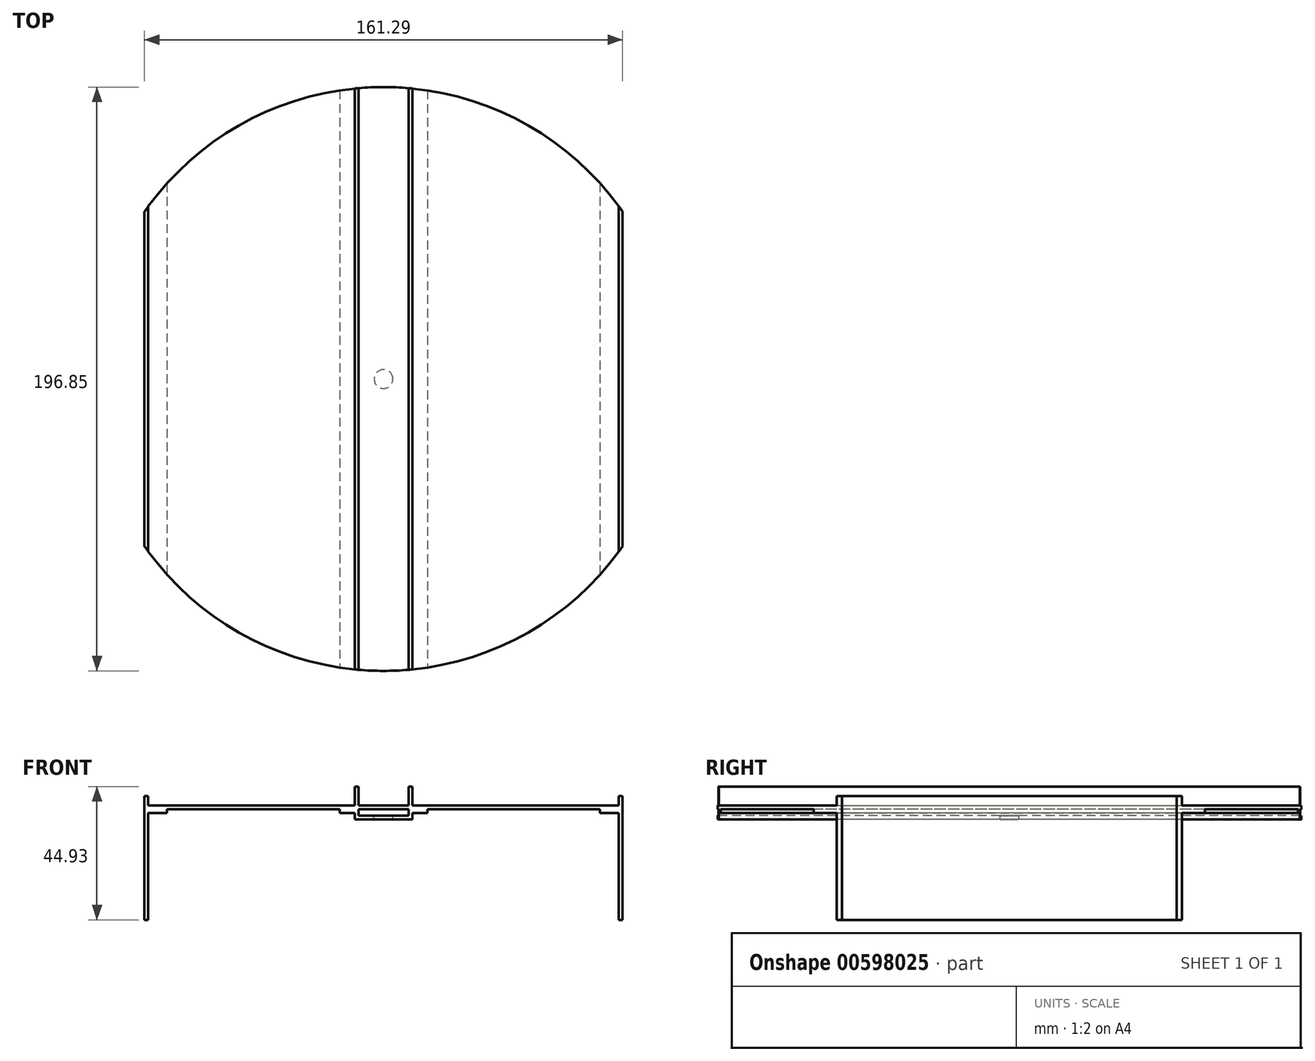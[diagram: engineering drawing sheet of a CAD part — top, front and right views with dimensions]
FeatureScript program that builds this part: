
annotation { "Feature Type Name" : "Feature", "Feature Type Description" : "" }
export const myFeature = defineFeature(function(context is Context, id is Id, definition is map)
    precondition{}
    {
        {
            var Q0;
            Q0=qCreatedBy(makeId("Top.planeOp"),FACE);
            var sketch = newSketch(context, id + "F0", { "sketchPlane" : qUnion([Q0])});
            skCircle(sketch, "E0", {"center": v(0, 0) * mm, "radius": 98.43 * mm, "construction": true});
            skArc(sketch, "E1", {"start": v(-79.38, 58.2) * mm, "mid": v(0, 98.43) * mm, "end": v(79.38, 58.2) * mm});
            skArc(sketch, "E2", {"start": v(79.38, -58.2) * mm, "mid": v(0, -98.43) * mm, "end": v(-79.38, -58.2) * mm});
            skLineSegment(sketch, "E3", {"start": v(-79.38, 58.2) * mm, "end": v(-79.38, -58.2) * mm});
            skLineSegment(sketch, "E4", {"start": v(79.38, 58.2) * mm, "end": v(79.38, -58.2) * mm});
            skLineSegment(sketch, "E5", {"start": v(0, 98.43) * mm, "end": v(0, -98.43) * mm, "construction": true});
            skLineSegment(sketch, "E6", {"start": v(-8.47, 98.06) * mm, "end": v(-8.47, -98.06) * mm});
            skLineSegment(sketch, "E7", {"start": v(-9.74, 97.94) * mm, "end": v(-9.74, -97.94) * mm});
            skLineSegment(sketch, "E8", {"start": v(8.47, 98.06) * mm, "end": v(8.47, -98.06) * mm});
            skLineSegment(sketch, "E9", {"start": v(9.74, 97.94) * mm, "end": v(9.74, -97.94) * mm});
            skArc(sketch, "E10", {"start": v(-73.14, 65.86) * mm, "mid": v(-69.6, 69.6) * mm, "end": v(-65.86, 73.14) * mm});
            skArc(sketch, "E11", {"start": v(66.5, 72.57) * mm, "mid": v(69.6, 69.6) * mm, "end": v(72.57, 66.5) * mm});
            skArc(sketch, "E12", {"start": v(18.66, -96.64) * mm, "mid": v(-25.47, 95.07) * mm, "end": v(32.16, -93.02) * mm});
            skArc(sketch, "E13", {"start": v(-18.63, -96.65) * mm, "mid": v(-25.47, -95.07) * mm, "end": v(-32.2, -93.01) * mm});
            skArc(sketch, "E14", {"start": v(-30.41, 93.6) * mm, "mid": v(-25.47, 95.07) * mm, "end": v(-20.46, 96.27) * mm});
            skArc(sketch, "E15", {"start": v(20.46, 96.27) * mm, "mid": v(25.47, 95.07) * mm, "end": v(30.41, 93.6) * mm});
            skArc(sketch, "E16", {"start": v(64.56, -74.3) * mm, "mid": v(-69.6, 69.6) * mm, "end": v(74.3, -64.56) * mm});
            skArc(sketch, "E17", {"start": v(-72.22, -66.87) * mm, "mid": v(-69.6, -69.6) * mm, "end": v(-66.87, -72.22) * mm});
            skLineSegment(sketch, "E18", {"start": v(-69.6, 69.6) * mm, "end": v(-69.6, -69.6) * mm, "construction": true});
            skLineSegment(sketch, "E19", {"start": v(-69.6, -69.6) * mm, "end": v(69.6, -69.6) * mm, "construction": true});
            skLineSegment(sketch, "E20", {"start": v(69.6, -69.6) * mm, "end": v(69.6, 69.6) * mm, "construction": true});
            skLineSegment(sketch, "E21", {"start": v(69.6, 69.6) * mm, "end": v(-69.6, 69.6) * mm, "construction": true});
            skLineSegment(sketch, "E22", {"start": v(-25.47, 95.07) * mm, "end": v(-25.47, -95.07) * mm, "construction": true});
            skLineSegment(sketch, "E23", {"start": v(-25.47, -95.07) * mm, "end": v(25.47, -95.07) * mm, "construction": true});
            skLineSegment(sketch, "E24", {"start": v(25.47, -95.07) * mm, "end": v(25.47, 95.07) * mm, "construction": true});
            skLineSegment(sketch, "E25", {"start": v(25.47, 95.07) * mm, "end": v(-25.47, 95.07) * mm, "construction": true});
            skLineSegment(sketch, "E26", {"start": v(0, 0) * mm, "end": v(-69.6, 69.6) * mm, "construction": true});
            skLineSegment(sketch, "E27", {"start": v(0, 0) * mm, "end": v(-25.47, 95.07) * mm, "construction": true});
            skLineSegment(sketch, "E28", {"start": v(-69.6, 69.6) * mm, "end": v(-52.3, 86.89) * mm, "construction": true});
            skLineSegment(sketch, "E29", {"start": v(-25.47, 95.07) * mm, "end": v(-17.64, 97.17) * mm, "construction": true});
            skLineSegment(sketch, "E30", {"start": v(25.47, 95.07) * mm, "end": v(35.03, 92.51) * mm, "construction": true});
            skLineSegment(sketch, "E31", {"start": v(69.6, 69.6) * mm, "end": v(84.24, 54.95) * mm, "construction": true});
            skLineSegment(sketch, "E32", {"start": v(69.6, -69.6) * mm, "end": v(50.03, -89.17) * mm, "construction": true});
            skLineSegment(sketch, "E33", {"start": v(25.47, -95.07) * mm, "end": v(7.54, -99.88) * mm, "construction": true});
            skLineSegment(sketch, "E34", {"start": v(-25.47, -95.07) * mm, "end": v(-73.92, -82.09) * mm, "construction": true});
            skLineSegment(sketch, "E35", {"start": v(-69.6, -69.6) * mm, "end": v(-126.46, -12.73) * mm, "construction": true});
            skLineSegment(sketch, "E36", {"start": v(0, 0) * mm, "end": v(-73.14, 65.86) * mm, "construction": true});
            skLineSegment(sketch, "E37", {"start": v(0, 0) * mm, "end": v(-30.41, 93.6) * mm, "construction": true});
            skLineSegment(sketch, "E38", {"start": v(0, 0) * mm, "end": v(30.41, 93.6) * mm, "construction": true});
            skLineSegment(sketch, "E39", {"start": v(0, 0) * mm, "end": v(72.57, 66.5) * mm, "construction": true});
            skLineSegment(sketch, "E40", {"start": v(0, 0) * mm, "end": v(74.3, -64.56) * mm, "construction": true});
            skLineSegment(sketch, "E41", {"start": v(0, 0) * mm, "end": v(32.16, -93.02) * mm, "construction": true});
            skLineSegment(sketch, "E42", {"start": v(0, 0) * mm, "end": v(-32.2, -93.01) * mm, "construction": true});
            skLineSegment(sketch, "E43", {"start": v(0, 0) * mm, "end": v(-72.22, -66.87) * mm, "construction": true});
            skLineSegment(sketch, "E44", {"start": v(0, 0) * mm, "end": v(25.47, 95.07) * mm, "construction": true});
            skLineSegment(sketch, "E45", {"start": v(0, 0) * mm, "end": v(69.6, 69.6) * mm, "construction": true});
            skLineSegment(sketch, "E46", {"start": v(0, 0) * mm, "end": v(69.6, -69.6) * mm, "construction": true});
            skLineSegment(sketch, "E47", {"start": v(0, 0) * mm, "end": v(25.47, -95.07) * mm, "construction": true});
            skLineSegment(sketch, "E48", {"start": v(0, 0) * mm, "end": v(-25.47, -95.07) * mm, "construction": true});
            skLineSegment(sketch, "E49", {"start": v(0, 0) * mm, "end": v(-69.6, -69.6) * mm, "construction": true});
            skLineSegment(sketch, "E50", {"start": v(-73.14, 65.86) * mm, "end": v(-69.82, 62.54) * mm});
            skLineSegment(sketch, "E51", {"start": v(-69.82, 62.54) * mm, "end": v(-62.54, 69.82) * mm});
            skLineSegment(sketch, "E52", {"start": v(-62.54, 69.82) * mm, "end": v(-65.86, 73.14) * mm});
            skLineSegment(sketch, "E53", {"start": v(-69.6, 69.6) * mm, "end": v(-67.89, 67.89) * mm, "construction": true});
            skLineSegment(sketch, "E54", {"start": v(-67.89, 67.89) * mm, "end": v(-66.18, 66.18) * mm, "construction": true});
            skLineSegment(sketch, "E55", {"start": v(-67.13, 71.98) * mm, "end": v(-64.97, 69.82) * mm});
            skLineSegment(sketch, "E56", {"start": v(-64.97, 69.82) * mm, "end": v(-69.82, 64.97) * mm});
            skLineSegment(sketch, "E57", {"start": v(-69.82, 64.97) * mm, "end": v(-71.98, 67.13) * mm});
            skLineSegment(sketch, "E58", {"start": v(-69.82, 64.97) * mm, "end": v(-71.04, 63.76) * mm, "construction": true});
            skLineSegment(sketch, "E59", {"start": v(-64.97, 69.82) * mm, "end": v(-63.76, 71.04) * mm, "construction": true});
            skLineSegment(sketch, "E60", {"start": v(-69.82, 64.97) * mm, "end": v(-68.6, 63.76) * mm, "construction": true});
            skLineSegment(sketch, "E61", {"start": v(-30.41, 93.6) * mm, "end": v(-29.2, 89.07) * mm});
            skLineSegment(sketch, "E62", {"start": v(-29.2, 89.07) * mm, "end": v(-19.25, 91.74) * mm});
            skLineSegment(sketch, "E63", {"start": v(-19.25, 91.74) * mm, "end": v(-20.46, 96.27) * mm});
            skLineSegment(sketch, "E64", {"start": v(-28.77, 94.13) * mm, "end": v(-27.98, 91.18) * mm});
            skLineSegment(sketch, "E65", {"start": v(-27.98, 91.18) * mm, "end": v(-21.36, 92.96) * mm});
            skLineSegment(sketch, "E66", {"start": v(-21.36, 92.96) * mm, "end": v(-22.15, 95.9) * mm});
            skLineSegment(sketch, "E67", {"start": v(-27.98, 91.18) * mm, "end": v(-29.65, 90.74) * mm, "construction": true});
            skLineSegment(sketch, "E68", {"start": v(-27.98, 91.18) * mm, "end": v(-27.54, 89.52) * mm, "construction": true});
            skLineSegment(sketch, "E69", {"start": v(-21.36, 92.96) * mm, "end": v(-19.7, 93.4) * mm, "construction": true});
            skLineSegment(sketch, "E70", {"start": v(20.46, 96.27) * mm, "end": v(19.25, 91.74) * mm});
            skLineSegment(sketch, "E71", {"start": v(19.25, 91.74) * mm, "end": v(29.2, 89.07) * mm});
            skLineSegment(sketch, "E72", {"start": v(29.2, 89.07) * mm, "end": v(30.41, 93.6) * mm});
            skLineSegment(sketch, "E73", {"start": v(22.15, 95.9) * mm, "end": v(21.36, 92.96) * mm});
            skLineSegment(sketch, "E74", {"start": v(21.36, 92.96) * mm, "end": v(27.98, 91.18) * mm});
            skLineSegment(sketch, "E75", {"start": v(27.98, 91.18) * mm, "end": v(28.77, 94.13) * mm});
            skLineSegment(sketch, "E76", {"start": v(21.36, 92.96) * mm, "end": v(19.7, 93.4) * mm, "construction": true});
            skLineSegment(sketch, "E77", {"start": v(27.98, 91.18) * mm, "end": v(29.65, 90.74) * mm, "construction": true});
            skLineSegment(sketch, "E78", {"start": v(21.36, 92.96) * mm, "end": v(20.91, 91.3) * mm, "construction": true});
            skSolve(sketch);
        }
        {
            var Q0;
            {var subQ0=sQuery(id+"F0.wireOp",EDGE,"E3");Q0=makeQuery(id+"F0.imprint","IMPRINT",FACE,{"disambiguationData":[TD([[makeQuery(id+"F0.imprint","IMPRINT",EDGE,{"derivedFrom":subQ0}),1.0]])]});}
            var Q1;
            {var subQ0=sQuery(id+"F0.wireOp",EDGE,"E4");Q1=makeQuery(id+"F0.imprint","IMPRINT",FACE,{"disambiguationData":[TD([[makeQuery(id+"F0.imprint","IMPRINT",EDGE,{"derivedFrom":subQ0}),-1.0]])]});}
            var Q2;
            {var subQ0=sQuery(id+"F0.wireOp",EDGE,"E6");Q2=makeQuery(id+"F0.imprint","IMPRINT",FACE,{"disambiguationData":[TD([[makeQuery(id+"F0.imprint","IMPRINT",EDGE,{"derivedFrom":subQ0}),1.0]])]});}
            var Q3;
            {var subQ0=sQuery(id+"F0.wireOp",EDGE,"E6");Q3=makeQuery(id+"F0.imprint","IMPRINT",FACE,{"disambiguationData":[TD([[makeQuery(id+"F0.imprint","IMPRINT",EDGE,{"derivedFrom":subQ0}),-1.0]])]});}
            var Q4;
            {var subQ0=sQuery(id+"F0.wireOp",EDGE,"E8");Q4=makeQuery(id+"F0.imprint","IMPRINT",FACE,{"disambiguationData":[TD([[makeQuery(id+"F0.imprint","IMPRINT",EDGE,{"derivedFrom":subQ0}),1.0]])]});}
            var Q5;
            {var subQ0=sQuery(id+"F0.wireOp",EDGE,"E55");Q5=makeQuery(id+"F0.imprint","IMPRINT",FACE,{"disambiguationData":[TD([[makeQuery(id+"F0.imprint","IMPRINT",EDGE,{"derivedFrom":subQ0}),-1.0]])]});}
            var Q6;
            {var subQ0=sQuery(id+"F0.wireOp",EDGE,"E50");Q6=makeQuery(id+"F0.imprint","IMPRINT",FACE,{"disambiguationData":[TD([[makeQuery(id+"F0.imprint","IMPRINT",EDGE,{"derivedFrom":subQ0}),1.0]])]});}
            var Q7;
            {var subQ0=sQuery(id+"F0.wireOp",EDGE,"E61");Q7=makeQuery(id+"F0.imprint","IMPRINT",FACE,{"disambiguationData":[TD([[makeQuery(id+"F0.imprint","IMPRINT",EDGE,{"derivedFrom":subQ0}),1.0]])]});}
            var Q8;
            {var subQ0=sQuery(id+"F0.wireOp",EDGE,"E64");Q8=makeQuery(id+"F0.imprint","IMPRINT",FACE,{"disambiguationData":[TD([[makeQuery(id+"F0.imprint","IMPRINT",EDGE,{"derivedFrom":subQ0}),1.0]])]});}
            var Q9;
            {var subQ0=sQuery(id+"F0.wireOp",EDGE,"E70");Q9=makeQuery(id+"F0.imprint","IMPRINT",FACE,{"disambiguationData":[TD([[makeQuery(id+"F0.imprint","IMPRINT",EDGE,{"derivedFrom":subQ0}),1.0]])]});}
            var Q10;
            {var subQ0=sQuery(id+"F0.wireOp",EDGE,"E73");Q10=makeQuery(id+"F0.imprint","IMPRINT",FACE,{"disambiguationData":[TD([[makeQuery(id+"F0.imprint","IMPRINT",EDGE,{"derivedFrom":subQ0}),1.0]])]});}
            extrude(context, id + "F1", {"entities" : qUnion([Q0, Q1, Q2, Q3, Q4, Q5, Q6, Q7, Q8, Q9, Q10]), "depth" : 1.27 * mm, "offsetDistance" : 25.4 * mm});
        }
        {
            var Q0;
            {var subQ0=sQuery(id+"F0.wireOp",EDGE,"E6");Q0=makeQuery(id+"F0.imprint","IMPRINT",FACE,{"disambiguationData":[TD([[makeQuery(id+"F0.imprint","IMPRINT",EDGE,{"derivedFrom":subQ0}),-1.0]])]});}
            var Q1;
            {var subQ0=sQuery(id+"F0.wireOp",EDGE,"E8");Q1=makeQuery(id+"F0.imprint","IMPRINT",FACE,{"disambiguationData":[TD([[makeQuery(id+"F0.imprint","IMPRINT",EDGE,{"derivedFrom":subQ0}),1.0]])]});}
            extrude(context, id + "F2", {"entities" : qUnion([Q0, Q1]), "operationType" : NewBodyOperationType.ADD, "depth" : 7.7 * mm, "offsetDistance" : 25.4 * mm});
        }
        {
            var Q0;
            Q0=qCreatedBy(makeId("Front.planeOp"),FACE);
            var sketch = newSketch(context, id + "F3", { "sketchPlane" : qUnion([Q0])});
            skLineSegment(sketch, "E79", {"start": v(0, 37.45) * mm, "end": v(0, -50.2) * mm, "construction": true});
            skSolve(sketch);
        }
        {
            var Q0;
            Q0=qCreatedBy(makeId("Top.planeOp"),FACE);
            var sketch = newSketch(context, id + "F4", { "sketchPlane" : qUnion([Q0])});
            skCircle(sketch, "E80", {"center": v(0, 0) * mm, "radius": 98.43 * mm, "construction": true});
            skLineSegment(sketch, "E81", {"start": v(0, 0) * mm, "end": v(-79.38, 0) * mm, "construction": true});
            skLineSegment(sketch, "E82", {"start": v(0, 0) * mm, "end": v(79.38, 0) * mm, "construction": true});
            skLineSegment(sketch, "E83", {"start": v(-79.38, 0) * mm, "end": v(-98.43, 0) * mm, "construction": true});
            skLineSegment(sketch, "E84", {"start": v(79.38, 0) * mm, "end": v(98.43, 0) * mm, "construction": true});
            skLineSegment(sketch, "E85", {"start": v(-79.38, 0) * mm, "end": v(-73.28, 0) * mm, "construction": true});
            skLineSegment(sketch, "E86", {"start": v(79.38, 0) * mm, "end": v(73.28, 0) * mm, "construction": true});
            skLineSegment(sketch, "E87", {"start": v(-79.38, 0) * mm, "end": v(-79.38, 58.2) * mm});
            skLineSegment(sketch, "E88", {"start": v(-79.38, 0) * mm, "end": v(-79.38, -58.2) * mm});
            skLineSegment(sketch, "E89", {"start": v(-73.28, 0) * mm, "end": v(-73.28, -65.7) * mm});
            skLineSegment(sketch, "E90", {"start": v(-73.28, 0) * mm, "end": v(-73.28, 65.7) * mm});
            skLineSegment(sketch, "E91", {"start": v(73.28, 0) * mm, "end": v(73.28, 65.7) * mm});
            skLineSegment(sketch, "E92", {"start": v(79.38, 0) * mm, "end": v(79.38, 58.2) * mm});
            skLineSegment(sketch, "E93", {"start": v(79.38, 0) * mm, "end": v(79.38, -58.2) * mm});
            skLineSegment(sketch, "E94", {"start": v(73.28, 0) * mm, "end": v(73.28, -65.7) * mm});
            skArc(sketch, "E95", {"start": v(-79.38, 58.2) * mm, "mid": v(-76.42, 62.03) * mm, "end": v(-73.28, 65.7) * mm});
            skArc(sketch, "E96", {"start": v(-79.38, -58.2) * mm, "mid": v(-76.42, -62.03) * mm, "end": v(-73.28, -65.7) * mm});
            skArc(sketch, "E97", {"start": v(73.28, 65.7) * mm, "mid": v(76.42, 62.03) * mm, "end": v(79.38, 58.2) * mm});
            skArc(sketch, "E98", {"start": v(73.28, -65.7) * mm, "mid": v(76.42, -62.03) * mm, "end": v(79.38, -58.2) * mm});
            skLineSegment(sketch, "E99", {"start": v(-79.38, 0) * mm, "end": v(-80.65, 0) * mm, "construction": true});
            skLineSegment(sketch, "E100", {"start": v(79.38, 0) * mm, "end": v(80.65, 0) * mm, "construction": true});
            skLineSegment(sketch, "E101", {"start": v(-80.65, 0) * mm, "end": v(-80.65, 56.43) * mm});
            skLineSegment(sketch, "E102", {"start": v(-80.65, 0) * mm, "end": v(-80.65, -56.43) * mm});
            skLineSegment(sketch, "E103", {"start": v(80.65, 0) * mm, "end": v(80.65, -56.43) * mm});
            skLineSegment(sketch, "E104", {"start": v(80.65, 0) * mm, "end": v(80.65, 56.43) * mm});
            skArc(sketch, "E105", {"start": v(79.38, 58.2) * mm, "mid": v(80.01, 57.32) * mm, "end": v(80.65, 56.43) * mm});
            skArc(sketch, "E106", {"start": v(79.38, -58.2) * mm, "mid": v(80.01, -57.32) * mm, "end": v(80.65, -56.43) * mm});
            skArc(sketch, "E107", {"start": v(-79.38, -58.2) * mm, "mid": v(-80.01, -57.32) * mm, "end": v(-80.65, -56.43) * mm});
            skArc(sketch, "E108", {"start": v(-80.65, 56.43) * mm, "mid": v(-80.01, 57.32) * mm, "end": v(-79.37, 58.2) * mm});
            skSolve(sketch);
        }
        {
            var Q0;
            Q0=makeQuery(id+"F4.imprint","IMPRINT",FACE,{"disambiguationData":[TD([[makeQuery(id+"F4.imprint","IMPRINT",EDGE,{"derivedFrom":sQuery(id+"F4.wireOp",EDGE,"E87")}),-1.0]])]});
            var Q1;
            Q1=makeQuery(id+"F4.imprint","IMPRINT",FACE,{"disambiguationData":[TD([[makeQuery(id+"F4.imprint","IMPRINT",EDGE,{"derivedFrom":sQuery(id+"F4.wireOp",EDGE,"E91")}),-1.0]])]});
            extrude(context, id + "F5", {"entities" : qUnion([Q0, Q1]), "oppositeDirection" : true, "depth" : 1.27 * mm, "offsetDistance" : 25.4 * mm});
        }
        {
            var Q0;
            Q0=makeQuery(id+"F4.imprint","IMPRINT",FACE,{"disambiguationData":[TD([[makeQuery(id+"F4.imprint","IMPRINT",EDGE,{"derivedFrom":sQuery(id+"F4.wireOp",EDGE,"E87")}),1.0]])]});
            var Q1;
            Q1=makeQuery(id+"F4.imprint","IMPRINT",FACE,{"disambiguationData":[TD([[makeQuery(id+"F4.imprint","IMPRINT",EDGE,{"derivedFrom":sQuery(id+"F4.wireOp",EDGE,"E92")}),-1.0]])]});
            extrude(context, id + "F6", {"entities" : qUnion([Q0, Q1]), "operationType" : NewBodyOperationType.ADD, "depth" : 4.5 * mm, "offsetDistance" : 25.4 * mm, "hasSecondDirection" : true, "secondDirectionOppositeDirection" : true, "secondDirectionDepth" : 28.5 * mm});
        }
        {
            var Q0;
            {var subQ1=sQuery(id+"F0.wireOp",EDGE,"E3");Q0=makeQuery(id+"F0.imprint","IMPRINT",FACE,{"disambiguationData":[TD([[makeQuery(id+"F0.imprint","IMPRINT",EDGE,{"derivedFrom":subQ1}),1.0]])]});}
            var Q1;
            {var subQ0=sQuery(id+"F0.wireOp",EDGE,"E6");Q1=makeQuery(id+"F0.imprint","IMPRINT",FACE,{"disambiguationData":[TD([[makeQuery(id+"F0.imprint","IMPRINT",EDGE,{"derivedFrom":subQ0}),1.0]])]});}
            var Q2;
            {var subQ0=sQuery(id+"F0.wireOp",EDGE,"E6");Q2=makeQuery(id+"F0.imprint","IMPRINT",FACE,{"disambiguationData":[TD([[makeQuery(id+"F0.imprint","IMPRINT",EDGE,{"derivedFrom":subQ0}),-1.0]])]});}
            var Q3;
            {var subQ0=sQuery(id+"F0.wireOp",EDGE,"E8");Q3=makeQuery(id+"F0.imprint","IMPRINT",FACE,{"disambiguationData":[TD([[makeQuery(id+"F0.imprint","IMPRINT",EDGE,{"derivedFrom":subQ0}),1.0]])]});}
            var Q4;
            {var subQ3=sQuery(id+"F0.wireOp",EDGE,"E4");Q4=makeQuery(id+"F0.imprint","IMPRINT",FACE,{"disambiguationData":[TD([[makeQuery(id+"F0.imprint","IMPRINT",EDGE,{"derivedFrom":subQ3}),-1.0]])]});}
            var Q5;
            {var subQ0=sQuery(id+"F0.wireOp",EDGE,"E55");Q5=makeQuery(id+"F0.imprint","IMPRINT",FACE,{"disambiguationData":[TD([[makeQuery(id+"F0.imprint","IMPRINT",EDGE,{"derivedFrom":subQ0}),-1.0]])]});}
            var Q6;
            {var subQ0=sQuery(id+"F0.wireOp",EDGE,"E50");Q6=makeQuery(id+"F0.imprint","IMPRINT",FACE,{"disambiguationData":[TD([[makeQuery(id+"F0.imprint","IMPRINT",EDGE,{"derivedFrom":subQ0}),1.0]])]});}
            var Q7;
            {var subQ0=sQuery(id+"F0.wireOp",EDGE,"E64");Q7=makeQuery(id+"F0.imprint","IMPRINT",FACE,{"disambiguationData":[TD([[makeQuery(id+"F0.imprint","IMPRINT",EDGE,{"derivedFrom":subQ0}),1.0]])]});}
            var Q8;
            {var subQ0=sQuery(id+"F0.wireOp",EDGE,"E61");Q8=makeQuery(id+"F0.imprint","IMPRINT",FACE,{"disambiguationData":[TD([[makeQuery(id+"F0.imprint","IMPRINT",EDGE,{"derivedFrom":subQ0}),1.0]])]});}
            var Q9;
            {var subQ0=sQuery(id+"F0.wireOp",EDGE,"E73");Q9=makeQuery(id+"F0.imprint","IMPRINT",FACE,{"disambiguationData":[TD([[makeQuery(id+"F0.imprint","IMPRINT",EDGE,{"derivedFrom":subQ0}),1.0]])]});}
            var Q10;
            {var subQ0=sQuery(id+"F0.wireOp",EDGE,"E70");Q10=makeQuery(id+"F0.imprint","IMPRINT",FACE,{"disambiguationData":[TD([[makeQuery(id+"F0.imprint","IMPRINT",EDGE,{"derivedFrom":subQ0}),1.0]])]});}
            extrude(context, id + "F7", {"entities" : qUnion([Q0, Q1, Q2, Q3, Q4, Q5, Q6, Q7, Q8, Q9, Q10]), "depth" : 1.27 * mm, "offsetDistance" : 25.4 * mm});
        }
        {
            var Q0;
            Q0=makeQuery(id+"F4.imprint","IMPRINT",FACE,{"disambiguationData":[TD([[makeQuery(id+"F4.imprint","IMPRINT",EDGE,{"derivedFrom":sQuery(id+"F4.wireOp",EDGE,"E87")}),-1.0]])]});
            var Q1;
            Q1=makeQuery(id+"F4.imprint","IMPRINT",FACE,{"disambiguationData":[TD([[makeQuery(id+"F4.imprint","IMPRINT",EDGE,{"derivedFrom":sQuery(id+"F4.wireOp",EDGE,"E91")}),-1.0]])]});
            extrude(context, id + "F8", {"entities" : qUnion([Q0, Q1]), "oppositeDirection" : true, "depth" : 1.27 * mm, "offsetDistance" : 25.4 * mm});
        }
        {
            var Q0;
            Q0=makeQuery(id+"F4.imprint","IMPRINT",FACE,{"disambiguationData":[TD([[makeQuery(id+"F4.imprint","IMPRINT",EDGE,{"derivedFrom":sQuery(id+"F4.wireOp",EDGE,"E87")}),1.0]])]});
            var Q1;
            Q1=makeQuery(id+"F4.imprint","IMPRINT",FACE,{"disambiguationData":[TD([[makeQuery(id+"F4.imprint","IMPRINT",EDGE,{"derivedFrom":sQuery(id+"F4.wireOp",EDGE,"E92")}),-1.0]])]});
            extrude(context, id + "F9", {"entities" : qUnion([Q0, Q1]), "operationType" : NewBodyOperationType.ADD, "depth" : 4.5 * mm, "offsetDistance" : 25.4 * mm, "hasSecondDirection" : true, "secondDirectionOppositeDirection" : true, "secondDirectionDepth" : 28.5 * mm});
        }
        {
            var Q0;
            Q0=makeQuery(id+"F4.imprint","IMPRINT",FACE,{"disambiguationData":[TD([[makeQuery(id+"F4.imprint","IMPRINT",EDGE,{"derivedFrom":sQuery(id+"F4.wireOp",EDGE,"E87")}),-1.0]])]});
            var Q1;
            Q1=makeQuery(id+"F4.imprint","IMPRINT",FACE,{"disambiguationData":[TD([[makeQuery(id+"F4.imprint","IMPRINT",EDGE,{"derivedFrom":sQuery(id+"F4.wireOp",EDGE,"E91")}),-1.0]])]});
            extrude(context, id + "F10", {"entities" : qUnion([Q0, Q1]), "oppositeDirection" : true, "depth" : 1.27 * mm, "offsetDistance" : 25.4 * mm});
        }
        {
            var Q0;
            Q0=makeQuery(id+"F4.imprint","IMPRINT",FACE,{"disambiguationData":[TD([[makeQuery(id+"F4.imprint","IMPRINT",EDGE,{"derivedFrom":sQuery(id+"F4.wireOp",EDGE,"E87")}),1.0]])]});
            var Q1;
            Q1=makeQuery(id+"F4.imprint","IMPRINT",FACE,{"disambiguationData":[TD([[makeQuery(id+"F4.imprint","IMPRINT",EDGE,{"derivedFrom":sQuery(id+"F4.wireOp",EDGE,"E92")}),-1.0]])]});
            extrude(context, id + "F11", {"entities" : qUnion([Q0, Q1]), "operationType" : NewBodyOperationType.ADD, "depth" : 3.45 * mm, "offsetDistance" : 25.4 * mm, "hasSecondDirection" : true, "secondDirectionOppositeDirection" : true, "secondDirectionDepth" : 30.36 * mm});
        }
        {
            var Q0;
            Q0=makeQuery(id+"F4.imprint","IMPRINT",FACE,{"disambiguationData":[TD([[makeQuery(id+"F4.imprint","IMPRINT",EDGE,{"derivedFrom":sQuery(id+"F4.wireOp",EDGE,"E87")}),-1.0]])]});
            var Q1;
            Q1=makeQuery(id+"F4.imprint","IMPRINT",FACE,{"disambiguationData":[TD([[makeQuery(id+"F4.imprint","IMPRINT",EDGE,{"derivedFrom":sQuery(id+"F4.wireOp",EDGE,"E91")}),-1.0]])]});
            extrude(context, id + "F12", {"entities" : qUnion([Q0, Q1]), "oppositeDirection" : true, "depth" : 1.27 * mm, "offsetDistance" : 25.4 * mm});
        }
        {
            var Q0;
            Q0=makeQuery(id+"F4.imprint","IMPRINT",FACE,{"disambiguationData":[TD([[makeQuery(id+"F4.imprint","IMPRINT",EDGE,{"derivedFrom":sQuery(id+"F4.wireOp",EDGE,"E87")}),1.0]])]});
            var Q1;
            Q1=makeQuery(id+"F4.imprint","IMPRINT",FACE,{"disambiguationData":[TD([[makeQuery(id+"F4.imprint","IMPRINT",EDGE,{"derivedFrom":sQuery(id+"F4.wireOp",EDGE,"E92")}),-1.0]])]});
            extrude(context, id + "F13", {"entities" : qUnion([Q0, Q1]), "operationType" : NewBodyOperationType.ADD, "depth" : 3.45 * mm, "offsetDistance" : 25.4 * mm, "hasSecondDirection" : true, "secondDirectionOppositeDirection" : true, "secondDirectionDepth" : 30.36 * mm});
        }
        {
            var Q0;
            Q0=makeQuery(id+"F4.imprint","IMPRINT",FACE,{"disambiguationData":[TD([[makeQuery(id+"F4.imprint","IMPRINT",EDGE,{"derivedFrom":sQuery(id+"F4.wireOp",EDGE,"E87")}),-1.0]])]});
            var Q1;
            Q1=makeQuery(id+"F4.imprint","IMPRINT",FACE,{"disambiguationData":[TD([[makeQuery(id+"F4.imprint","IMPRINT",EDGE,{"derivedFrom":sQuery(id+"F4.wireOp",EDGE,"E91")}),-1.0]])]});
            extrude(context, id + "F14", {"entities" : qUnion([Q0, Q1]), "oppositeDirection" : true, "depth" : 1.27 * mm, "offsetDistance" : 25.4 * mm});
        }
        {
            var Q0;
            Q0=makeQuery(id+"F4.imprint","IMPRINT",FACE,{"disambiguationData":[TD([[makeQuery(id+"F4.imprint","IMPRINT",EDGE,{"derivedFrom":sQuery(id+"F4.wireOp",EDGE,"E87")}),1.0]])]});
            var Q1;
            Q1=makeQuery(id+"F4.imprint","IMPRINT",FACE,{"disambiguationData":[TD([[makeQuery(id+"F4.imprint","IMPRINT",EDGE,{"derivedFrom":sQuery(id+"F4.wireOp",EDGE,"E92")}),-1.0]])]});
            extrude(context, id + "F15", {"entities" : qUnion([Q0, Q1]), "operationType" : NewBodyOperationType.ADD, "depth" : 3.45 * mm, "offsetDistance" : 25.4 * mm, "hasSecondDirection" : true, "secondDirectionOppositeDirection" : true, "secondDirectionDepth" : 30.9 * mm});
        }
        {
            var Q0;
            Q0=qCreatedBy(makeId("Top.planeOp"),FACE);
            var sketch = newSketch(context, id + "F16", { "sketchPlane" : qUnion([Q0])});
            skCircle(sketch, "E109", {"center": v(0, 0) * mm, "radius": 98.43 * mm, "construction": true});
            skLineSegment(sketch, "E110", {"start": v(0, 98.43) * mm, "end": v(0, -98.43) * mm, "construction": true});
            skLineSegment(sketch, "E111", {"start": v(-98.43, 0) * mm, "end": v(98.43, 0) * mm, "construction": true});
            skLineSegment(sketch, "E112", {"start": v(-8.47, 98.06) * mm, "end": v(-8.47, -98.06) * mm});
            skLineSegment(sketch, "E113", {"start": v(8.47, 98.06) * mm, "end": v(8.47, -98.06) * mm});
            skLineSegment(sketch, "E114", {"start": v(-79.38, 58.2) * mm, "end": v(-79.38, -58.2) * mm});
            skLineSegment(sketch, "E115", {"start": v(79.38, 58.2) * mm, "end": v(79.38, -58.2) * mm});
            skArc(sketch, "E116", {"start": v(-79.38, 58.2) * mm, "mid": v(-48.23, 85.8) * mm, "end": v(-8.47, 98.06) * mm});
            skArc(sketch, "E117", {"start": v(8.47, 98.06) * mm, "mid": v(48.23, 85.8) * mm, "end": v(79.38, 58.2) * mm});
            skArc(sketch, "E118", {"start": v(79.38, -58.2) * mm, "mid": v(48.23, -85.8) * mm, "end": v(8.47, -98.06) * mm});
            skArc(sketch, "E119", {"start": v(-8.47, -98.06) * mm, "mid": v(-48.23, -85.8) * mm, "end": v(-79.38, -58.2) * mm});
            skLineSegment(sketch, "E120", {"start": v(-14.82, 97.3) * mm, "end": v(-14.82, -97.3) * mm});
            skLineSegment(sketch, "E121", {"start": v(14.82, 97.3) * mm, "end": v(14.82, -97.3) * mm});
            skLineSegment(sketch, "E122", {"start": v(-9.74, 97.94) * mm, "end": v(-9.74, -97.94) * mm});
            skLineSegment(sketch, "E123", {"start": v(9.74, 97.94) * mm, "end": v(9.74, -97.94) * mm});
            skLineSegment(sketch, "E124", {"start": v(73.03, 66) * mm, "end": v(73.03, -66) * mm});
            skLineSegment(sketch, "E125", {"start": v(80.65, 56.43) * mm, "end": v(80.65, -56.43) * mm});
            skLineSegment(sketch, "E126", {"start": v(-73.03, 66) * mm, "end": v(-73.03, -66) * mm});
            skLineSegment(sketch, "E127", {"start": v(-80.65, 56.43) * mm, "end": v(-80.65, -56.43) * mm});
            skArc(sketch, "E128", {"start": v(79.38, 58.2) * mm, "mid": v(80.01, 57.32) * mm, "end": v(80.65, 56.43) * mm});
            skArc(sketch, "E129", {"start": v(80.65, -56.43) * mm, "mid": v(80.01, -57.32) * mm, "end": v(79.38, -58.2) * mm});
            skArc(sketch, "E130", {"start": v(-79.38, -58.2) * mm, "mid": v(-80.01, -57.32) * mm, "end": v(-80.65, -56.43) * mm});
            skArc(sketch, "E131", {"start": v(-80.65, 56.43) * mm, "mid": v(-80.01, 57.32) * mm, "end": v(-79.37, 58.2) * mm});
            skArc(sketch, "E132", {"start": v(-8.47, 98.06) * mm, "mid": v(0, 98.43) * mm, "end": v(8.47, 98.06) * mm});
            skArc(sketch, "E133", {"start": v(-8.47, -98.06) * mm, "mid": v(0, -98.43) * mm, "end": v(8.47, -98.06) * mm});
            skCircle(sketch, "E134", {"center": v(0, 0) * mm, "radius": 3.18 * mm});
            skSolve(sketch);
        }
        {
            var Q0;
            {var subQ0=sQuery(id+"F16.wireOp",EDGE,"E120");Q0=makeQuery(id+"F16.imprint","IMPRINT",FACE,{"disambiguationData":[TD([[makeQuery(id+"F16.imprint","IMPRINT",EDGE,{"derivedFrom":subQ0}),-1.0]])]});}
            var Q1;
            {var subQ0=sQuery(id+"F16.wireOp",EDGE,"E121");Q1=makeQuery(id+"F16.imprint","IMPRINT",FACE,{"disambiguationData":[TD([[makeQuery(id+"F16.imprint","IMPRINT",EDGE,{"derivedFrom":subQ0}),1.0]])]});}
            var Q2;
            {var subQ0=sQuery(id+"F16.wireOp",EDGE,"E114");Q2=makeQuery(id+"F16.imprint","IMPRINT",FACE,{"disambiguationData":[TD([[makeQuery(id+"F16.imprint","IMPRINT",EDGE,{"derivedFrom":subQ0}),1.0]])]});}
            var Q3;
            {var subQ0=sQuery(id+"F16.wireOp",EDGE,"E120");Q3=makeQuery(id+"F16.imprint","IMPRINT",FACE,{"disambiguationData":[TD([[makeQuery(id+"F16.imprint","IMPRINT",EDGE,{"derivedFrom":subQ0}),1.0]])]});}
            var Q4;
            {var subQ0=sQuery(id+"F16.wireOp",EDGE,"E112");Q4=makeQuery(id+"F16.imprint","IMPRINT",FACE,{"disambiguationData":[TD([[makeQuery(id+"F16.imprint","IMPRINT",EDGE,{"derivedFrom":subQ0}),-1.0]])]});}
            var Q5;
            {var subQ0=sQuery(id+"F16.wireOp",EDGE,"E113");Q5=makeQuery(id+"F16.imprint","IMPRINT",FACE,{"disambiguationData":[TD([[makeQuery(id+"F16.imprint","IMPRINT",EDGE,{"derivedFrom":subQ0}),1.0]])]});}
            var Q6;
            {var subQ0=sQuery(id+"F16.wireOp",EDGE,"E121");Q6=makeQuery(id+"F16.imprint","IMPRINT",FACE,{"disambiguationData":[TD([[makeQuery(id+"F16.imprint","IMPRINT",EDGE,{"derivedFrom":subQ0}),-1.0]])]});}
            var Q7;
            {var subQ0=sQuery(id+"F16.wireOp",EDGE,"E115");Q7=makeQuery(id+"F16.imprint","IMPRINT",FACE,{"disambiguationData":[TD([[makeQuery(id+"F16.imprint","IMPRINT",EDGE,{"derivedFrom":subQ0}),-1.0]])]});}
            extrude(context, id + "F17", {"entities" : qUnion([Q0, Q1, Q2, Q3, Q4, Q5, Q6, Q7]), "depth" : 1.27 * mm, "offsetDistance" : 25.4 * mm});
        }
        {
            var Q0;
            {var subQ0=sQuery(id+"F16.wireOp",EDGE,"E114");Q0=makeQuery(id+"F16.imprint","IMPRINT",FACE,{"disambiguationData":[TD([[makeQuery(id+"F16.imprint","IMPRINT",EDGE,{"derivedFrom":subQ0}),1.0]])]});}
            var Q1;
            {var subQ0=sQuery(id+"F16.wireOp",EDGE,"E115");Q1=makeQuery(id+"F16.imprint","IMPRINT",FACE,{"disambiguationData":[TD([[makeQuery(id+"F16.imprint","IMPRINT",EDGE,{"derivedFrom":subQ0}),-1.0]])]});}
            extrude(context, id + "F18", {"entities" : qUnion([Q0, Q1]), "oppositeDirection" : true, "depth" : 1.27 * mm, "offsetDistance" : 25.4 * mm});
        }
        {
            var Q0;
            Q0=makeQuery(id+"F16.imprint","IMPRINT",FACE,{"disambiguationData":[TD([[makeQuery(id+"F16.imprint","IMPRINT",EDGE,{"derivedFrom":sQuery(id+"F16.wireOp",EDGE,"E114")}),-1.0]])]});
            var Q1;
            Q1=makeQuery(id+"F16.imprint","IMPRINT",FACE,{"disambiguationData":[TD([[makeQuery(id+"F16.imprint","IMPRINT",EDGE,{"derivedFrom":sQuery(id+"F16.wireOp",EDGE,"E115")}),1.0]])]});
            extrude(context, id + "F19", {"entities" : qUnion([Q0, Q1]), "operationType" : NewBodyOperationType.ADD, "depth" : 3.45 * mm, "offsetDistance" : 25.4 * mm, "hasSecondDirection" : true, "secondDirectionOppositeDirection" : true, "secondDirectionDepth" : 36.98 * mm});
        }
        {
            var Q0;
            {var subQ0=sQuery(id+"F16.wireOp",EDGE,"E120");Q0=makeQuery(id+"F16.imprint","IMPRINT",FACE,{"disambiguationData":[TD([[makeQuery(id+"F16.imprint","IMPRINT",EDGE,{"derivedFrom":subQ0}),1.0]])]});}
            var Q1;
            {var subQ0=sQuery(id+"F16.wireOp",EDGE,"E121");Q1=makeQuery(id+"F16.imprint","IMPRINT",FACE,{"disambiguationData":[TD([[makeQuery(id+"F16.imprint","IMPRINT",EDGE,{"derivedFrom":subQ0}),-1.0]])]});}
            extrude(context, id + "F20", {"entities" : qUnion([Q0, Q1]), "oppositeDirection" : true, "depth" : 1.27 * mm, "offsetDistance" : 25.4 * mm});
        }
        {
            var Q0;
            {var subQ0=sQuery(id+"F16.wireOp",EDGE,"E112");Q0=makeQuery(id+"F16.imprint","IMPRINT",FACE,{"disambiguationData":[TD([[makeQuery(id+"F16.imprint","IMPRINT",EDGE,{"derivedFrom":subQ0}),-1.0]])]});}
            var Q1;
            {var subQ0=sQuery(id+"F16.wireOp",EDGE,"E113");Q1=makeQuery(id+"F16.imprint","IMPRINT",FACE,{"disambiguationData":[TD([[makeQuery(id+"F16.imprint","IMPRINT",EDGE,{"derivedFrom":subQ0}),1.0]])]});}
            extrude(context, id + "F21", {"entities" : qUnion([Q0, Q1]), "operationType" : NewBodyOperationType.ADD, "oppositeDirection" : true, "depth" : 2.12 * mm, "offsetDistance" : 25.4 * mm});
        }
        {
            var Q0;
            Q0=makeQuery(id+"F16.imprint","IMPRINT",FACE,{"disambiguationData":[TD([[makeQuery(id+"F16.imprint","IMPRINT",EDGE,{"derivedFrom":sQuery(id+"F16.wireOp",EDGE,"E112")}),1.0]])]});
            var Q1;
            {var subQ0=sQuery(id+"F16.wireOp",EDGE,"E112");Q1=makeQuery(id+"F16.imprint","IMPRINT",FACE,{"disambiguationData":[TD([[makeQuery(id+"F16.imprint","IMPRINT",EDGE,{"derivedFrom":subQ0}),-1.0]])]});}
            var Q2;
            {var subQ0=sQuery(id+"F16.wireOp",EDGE,"E113");Q2=makeQuery(id+"F16.imprint","IMPRINT",FACE,{"disambiguationData":[TD([[makeQuery(id+"F16.imprint","IMPRINT",EDGE,{"derivedFrom":subQ0}),1.0]])]});}
            extrude(context, id + "F22", {"entities" : qUnion([Q0, Q1, Q2]), "operationType" : NewBodyOperationType.ADD, "oppositeDirection" : true, "depth" : 3.4 * mm, "offsetDistance" : 25.4 * mm, "hasSecondDirection" : true, "secondDirectionOppositeDirection" : true, "secondDirectionDepth" : 2.12 * mm});
        }
        {
            var Q0;
            Q0=qCreatedBy(makeId("Top.planeOp"),FACE);
            var sketch = newSketch(context, id + "F23", { "sketchPlane" : qUnion([Q0])});
            skCircle(sketch, "E135", {"center": v(0, 0) * mm, "radius": 98.43 * mm, "construction": true});
            skLineSegment(sketch, "E136", {"start": v(-98.43, 0) * mm, "end": v(98.43, 0) * mm, "construction": true});
            skLineSegment(sketch, "E137", {"start": v(0, 98.43) * mm, "end": v(0, -98.43) * mm, "construction": true});
            skLineSegment(sketch, "E138", {"start": v(-8.47, 98.06) * mm, "end": v(-8.47, -98.06) * mm});
            skLineSegment(sketch, "E139", {"start": v(8.47, 98.06) * mm, "end": v(8.47, -98.06) * mm});
            skLineSegment(sketch, "E140", {"start": v(79.38, 58.2) * mm, "end": v(79.38, -58.2) * mm});
            skLineSegment(sketch, "E141", {"start": v(-79.38, 58.2) * mm, "end": v(-79.37, -58.2) * mm});
            skLineSegment(sketch, "E142", {"start": v(-9.74, 97.94) * mm, "end": v(-9.74, -97.94) * mm});
            skLineSegment(sketch, "E143", {"start": v(-14.82, 97.3) * mm, "end": v(-14.82, -97.3) * mm});
            skLineSegment(sketch, "E144", {"start": v(9.74, 97.94) * mm, "end": v(9.74, -97.94) * mm});
            skLineSegment(sketch, "E145", {"start": v(14.82, 97.3) * mm, "end": v(14.82, -97.3) * mm});
            skLineSegment(sketch, "E146", {"start": v(73.03, 66) * mm, "end": v(73.03, -66) * mm});
            skLineSegment(sketch, "E147", {"start": v(80.65, 56.43) * mm, "end": v(80.65, -56.43) * mm});
            skLineSegment(sketch, "E148", {"start": v(-73.03, 66) * mm, "end": v(-73.02, -66) * mm});
            skLineSegment(sketch, "E149", {"start": v(-80.65, 56.43) * mm, "end": v(-80.65, -56.43) * mm});
            skArc(sketch, "E150", {"start": v(-80.65, 56.43) * mm, "mid": v(-49.18, 85.26) * mm, "end": v(-8.47, 98.06) * mm});
            skArc(sketch, "E151", {"start": v(8.47, 98.06) * mm, "mid": v(49.18, 85.26) * mm, "end": v(80.65, 56.43) * mm});
            skArc(sketch, "E152", {"start": v(-8.47, 98.06) * mm, "mid": v(0, 98.43) * mm, "end": v(8.47, 98.06) * mm});
            skArc(sketch, "E153", {"start": v(80.65, -56.43) * mm, "mid": v(0, -98.42) * mm, "end": v(-80.65, -56.43) * mm});
            skCircle(sketch, "E154", {"center": v(0, 0) * mm, "radius": 4.23 * mm});
            skSolve(sketch);
        }
        {
            var Q0;
            {var subQ0=sQuery(id+"F23.wireOp",EDGE,"E141");Q0=makeQuery(id+"F23.imprint","IMPRINT",FACE,{"disambiguationData":[TD([[makeQuery(id+"F23.imprint","IMPRINT",EDGE,{"derivedFrom":subQ0}),1.0]])]});}
            var Q1;
            {var subQ0=sQuery(id+"F23.wireOp",EDGE,"E143");Q1=makeQuery(id+"F23.imprint","IMPRINT",FACE,{"disambiguationData":[TD([[makeQuery(id+"F23.imprint","IMPRINT",EDGE,{"derivedFrom":subQ0}),-1.0]])]});}
            var Q2;
            {var subQ0=sQuery(id+"F23.wireOp",EDGE,"E142");Q2=makeQuery(id+"F23.imprint","IMPRINT",FACE,{"disambiguationData":[TD([[makeQuery(id+"F23.imprint","IMPRINT",EDGE,{"derivedFrom":subQ0}),-1.0]])]});}
            var Q3;
            {var subQ0=sQuery(id+"F23.wireOp",EDGE,"E138");Q3=makeQuery(id+"F23.imprint","IMPRINT",FACE,{"disambiguationData":[TD([[makeQuery(id+"F23.imprint","IMPRINT",EDGE,{"derivedFrom":subQ0}),-1.0]])]});}
            var Q4;
            {var subQ0=sQuery(id+"F23.wireOp",EDGE,"E139");Q4=makeQuery(id+"F23.imprint","IMPRINT",FACE,{"disambiguationData":[TD([[makeQuery(id+"F23.imprint","IMPRINT",EDGE,{"derivedFrom":subQ0}),1.0]])]});}
            var Q5;
            {var subQ0=sQuery(id+"F23.wireOp",EDGE,"E144");Q5=makeQuery(id+"F23.imprint","IMPRINT",FACE,{"disambiguationData":[TD([[makeQuery(id+"F23.imprint","IMPRINT",EDGE,{"derivedFrom":subQ0}),1.0]])]});}
            var Q6;
            {var subQ0=sQuery(id+"F23.wireOp",EDGE,"E145");Q6=makeQuery(id+"F23.imprint","IMPRINT",FACE,{"disambiguationData":[TD([[makeQuery(id+"F23.imprint","IMPRINT",EDGE,{"derivedFrom":subQ0}),1.0]])]});}
            var Q7;
            {var subQ0=sQuery(id+"F23.wireOp",EDGE,"E140");Q7=makeQuery(id+"F23.imprint","IMPRINT",FACE,{"disambiguationData":[TD([[makeQuery(id+"F23.imprint","IMPRINT",EDGE,{"derivedFrom":subQ0}),-1.0]])]});}
            extrude(context, id + "F24", {"entities" : qUnion([Q0, Q1, Q2, Q3, Q4, Q5, Q6, Q7]), "depth" : 1.27 * mm, "offsetDistance" : 25.4 * mm});
        }
        {
            var Q0;
            {var subQ0=sQuery(id+"F23.wireOp",EDGE,"E141");Q0=makeQuery(id+"F23.imprint","IMPRINT",FACE,{"disambiguationData":[TD([[makeQuery(id+"F23.imprint","IMPRINT",EDGE,{"derivedFrom":subQ0}),1.0]])]});}
            var Q1;
            {var subQ0=sQuery(id+"F23.wireOp",EDGE,"E140");Q1=makeQuery(id+"F23.imprint","IMPRINT",FACE,{"disambiguationData":[TD([[makeQuery(id+"F23.imprint","IMPRINT",EDGE,{"derivedFrom":subQ0}),-1.0]])]});}
            extrude(context, id + "F25", {"entities" : qUnion([Q0, Q1]), "oppositeDirection" : true, "depth" : 1.27 * mm, "offsetDistance" : 25.4 * mm});
        }
        {
            var Q0;
            {var subQ0=sQuery(id+"F23.wireOp",EDGE,"E141");Q0=makeQuery(id+"F23.imprint","IMPRINT",FACE,{"disambiguationData":[TD([[makeQuery(id+"F23.imprint","IMPRINT",EDGE,{"derivedFrom":subQ0}),-1.0]])]});}
            var Q1;
            {var subQ0=sQuery(id+"F23.wireOp",EDGE,"E140");Q1=makeQuery(id+"F23.imprint","IMPRINT",FACE,{"disambiguationData":[TD([[makeQuery(id+"F23.imprint","IMPRINT",EDGE,{"derivedFrom":subQ0}),1.0]])]});}
            extrude(context, id + "F26", {"entities" : qUnion([Q0, Q1]), "operationType" : NewBodyOperationType.ADD, "depth" : 3.45 * mm, "offsetDistance" : 25.4 * mm, "hasSecondDirection" : true, "secondDirectionOppositeDirection" : true, "secondDirectionDepth" : 37.24 * mm});
        }
        {
            var Q0;
            {var subQ0=sQuery(id+"F23.wireOp",EDGE,"E142");Q0=makeQuery(id+"F23.imprint","IMPRINT",FACE,{"disambiguationData":[TD([[makeQuery(id+"F23.imprint","IMPRINT",EDGE,{"derivedFrom":subQ0}),-1.0]])]});}
            var Q1;
            {var subQ0=sQuery(id+"F23.wireOp",EDGE,"E144");Q1=makeQuery(id+"F23.imprint","IMPRINT",FACE,{"disambiguationData":[TD([[makeQuery(id+"F23.imprint","IMPRINT",EDGE,{"derivedFrom":subQ0}),1.0]])]});}
            extrude(context, id + "F27", {"entities" : qUnion([Q0, Q1]), "oppositeDirection" : true, "depth" : 1.27 * mm, "offsetDistance" : 25.4 * mm});
        }
        {
            var Q0;
            {var subQ0=sQuery(id+"F23.wireOp",EDGE,"E138");Q0=makeQuery(id+"F23.imprint","IMPRINT",FACE,{"disambiguationData":[TD([[makeQuery(id+"F23.imprint","IMPRINT",EDGE,{"derivedFrom":subQ0}),-1.0]])]});}
            var Q1;
            {var subQ0=sQuery(id+"F23.wireOp",EDGE,"E139");Q1=makeQuery(id+"F23.imprint","IMPRINT",FACE,{"disambiguationData":[TD([[makeQuery(id+"F23.imprint","IMPRINT",EDGE,{"derivedFrom":subQ0}),1.0]])]});}
            extrude(context, id + "F28", {"entities" : qUnion([Q0, Q1]), "operationType" : NewBodyOperationType.ADD, "oppositeDirection" : true, "depth" : 3.4 * mm, "offsetDistance" : 25.4 * mm});
        }
        {
            var Q0;
            {var subQ0=sQuery(id+"F23.wireOp",EDGE,"E138");Q0=makeQuery(id+"F23.imprint","IMPRINT",FACE,{"disambiguationData":[TD([[makeQuery(id+"F23.imprint","IMPRINT",EDGE,{"derivedFrom":subQ0}),1.0]])]});}
            extrude(context, id + "F29", {"entities" : qUnion([Q0]), "operationType" : NewBodyOperationType.ADD, "oppositeDirection" : true, "depth" : 3.4 * mm, "offsetDistance" : 25.4 * mm, "hasSecondDirection" : true, "secondDirectionOppositeDirection" : true, "secondDirectionDepth" : 2.12 * mm});
        }
    });
